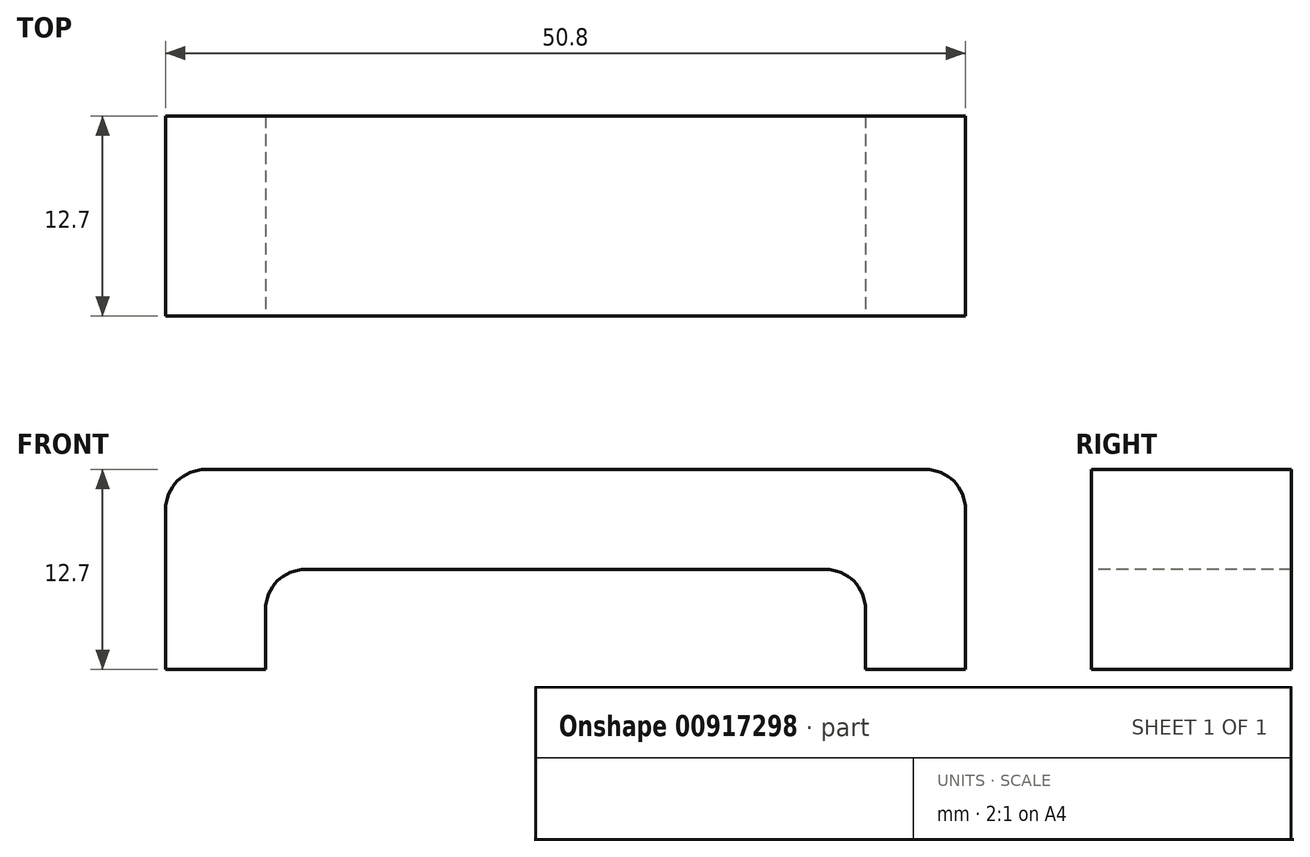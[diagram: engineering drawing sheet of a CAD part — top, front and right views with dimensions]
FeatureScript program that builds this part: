
annotation { "Feature Type Name" : "Feature", "Feature Type Description" : "" }
export const myFeature = defineFeature(function(context is Context, id is Id, definition is map)
    precondition{}
    {
        {
            var Q0;
            Q0=qCreatedBy(makeId("Front.planeOp"),FACE);
            var sketch = newSketch(context, id + "F0", { "sketchPlane" : qUnion([Q0])});
            skLineSegment(sketch, "E0", {"start": v(-25.4, -12.7) * mm, "end": v(-19.05, -12.7) * mm});
            skLineSegment(sketch, "E1", {"start": v(-19.05, -12.7) * mm, "end": v(-19.05, -6.35) * mm});
            skLineSegment(sketch, "E2", {"start": v(-19.05, -6.35) * mm, "end": v(19.05, -6.35) * mm});
            skLineSegment(sketch, "E3", {"start": v(19.05, -6.35) * mm, "end": v(19.05, -12.7) * mm});
            skLineSegment(sketch, "E4", {"start": v(19.05, -12.7) * mm, "end": v(25.4, -12.7) * mm});
            skLineSegment(sketch, "E5", {"start": v(25.4, -12.7) * mm, "end": v(25.4, 0) * mm});
            skLineSegment(sketch, "E6", {"start": v(25.4, 0) * mm, "end": v(-25.4, 0) * mm});
            skLineSegment(sketch, "E7", {"start": v(-25.4, 0) * mm, "end": v(-25.4, -12.7) * mm});
            skSolve(sketch);
        }
        {
            var Q0;
            Q0 = qSketchRegion(id + "F0", true);
            extrude(context, id + "F1", {"entities" : qUnion([Q0]), "oppositeDirection" : true, "depth" : 12.7 * mm, "offsetDistance" : 25.4 * mm});
        }
        {
            var Q0;
            Q0=makeQuery(id+"F1.opExtrude","SWEPT_EDGE",EDGE,{"disambiguationData":[OSD([sQuery(id+"F0.wireOp",EDGE,"E1"),sQuery(id+"F0.wireOp",EDGE,"E2")])]});
            var Q1;
            Q1=makeQuery(id+"F1.opExtrude","SWEPT_EDGE",EDGE,{"disambiguationData":[OSD([sQuery(id+"F0.wireOp",EDGE,"E2"),sQuery(id+"F0.wireOp",EDGE,"E3")])]});
            var Q2;
            Q2=makeQuery(id+"F1.opExtrude","SWEPT_EDGE",EDGE,{"disambiguationData":[OSD([sQuery(id+"F0.wireOp",EDGE,"E6"),sQuery(id+"F0.wireOp",EDGE,"E7")])]});
            var Q3;
            Q3=makeQuery(id+"F1.opExtrude","SWEPT_EDGE",EDGE,{"disambiguationData":[OSD([sQuery(id+"F0.wireOp",EDGE,"E5"),sQuery(id+"F0.wireOp",EDGE,"E6")])]});
            fillet(context, id + "F2", {"entities" : qUnion([Q0, Q1, Q2, Q3]), "radius" : 2.54 * mm, "tangentPropagation" : true, "allowEdgeOverflow" : false});
        }
    });
